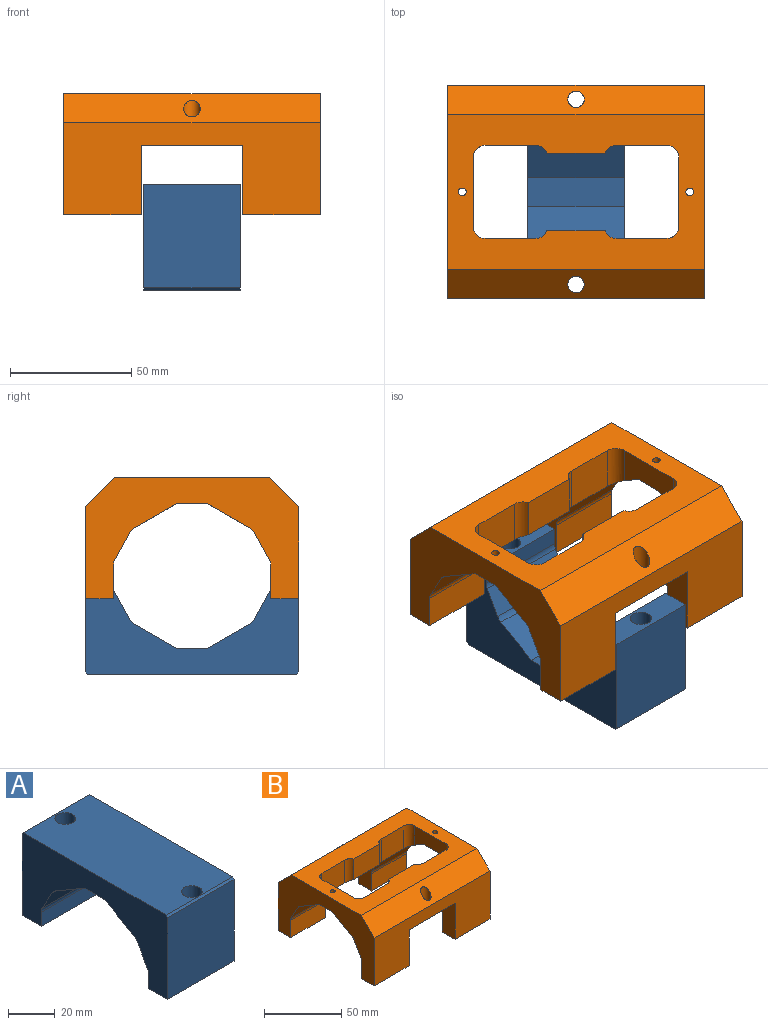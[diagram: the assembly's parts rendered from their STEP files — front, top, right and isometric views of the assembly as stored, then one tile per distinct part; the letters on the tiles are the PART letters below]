
ASSEMBLY  parts=2 mates=1
PART A: 22 faces, bbox 40x88x43.7 mm
  f0: plane 40x7.35mm, normal (0,-1,0), area 294.2mm2, adj f1,f15,f16,f17
  f1: plane 40x11.5mm, normal (0,0,-1), area 399.2mm2, adj f0,f2,f16,f17,f21
  f2: plane 42.65x40mm, normal (0,1,0), area 1706mm2, adj f1,f16,f17,f18
  f3: plane 86x40mm, normal (0,0,1), area 3318.4mm2, adj f16,f17,f18,f19,f20,f21
  f4: plane 42.65x40mm, normal (0,-1,0), area 1706mm2, adj f5,f16,f17,f19
  f5: plane 40x11.5mm, normal (0,0,-1), area 399.2mm2, adj f4,f6,f16,f17,f20
  f6: plane 40x7.35mm, normal (0,1,0), area 294.2mm2, adj f5,f7,f16,f17
  f7: cylinder r=5mm len=40mm, axis (-1,0,0), area 101.4mm2, adj f6,f8,f16,f17
  f8: plane 40x11.16mm, normal (0,0.87,-0.49), area 510.7mm2, adj f7,f9,f16,f17
  f9: cylinder r=5mm len=40mm, axis (-1,0,0), area 107.8mm2, adj f8,f10,f16,f17
  f10: plane 40x17.81mm, normal (0,0.5,-0.87), area 822.9mm2, adj f9,f11,f16,f17
  f11: plane 40x12mm, normal (0,0,-1), area 480mm2, adj f10,f12,f16,f17
  f12: plane 40x17.81mm, normal (0,-0.5,-0.87), area 822.9mm2, adj f11,f13,f16,f17
  f13: cylinder r=5mm len=40mm, axis (-1,0,0), area 107.8mm2, adj f12,f14,f16,f17
  f14: plane 40x11.16mm, normal (0,-0.87,-0.49), area 510.7mm2, adj f13,f15,f16,f17
  f15: cylinder r=5mm len=40mm, axis (-1,0,0), area 101.4mm2, adj f0,f14,f16,f17
  f16: plane 88x43.65mm, normal (1,0,0), area 2161.3mm2, adj f0,f1,f2,f3,f4,f5,f6,f7
  f17: plane 88x43.65mm, normal (-1,0,0), area 2161.3mm2, adj f0,f1,f2,f3,f4,f5,f6,f7
  f18: plane 40x1mm, normal (0,0.71,0.71), area 56.6mm2, adj f2,f3,f16,f17
  f19: plane 40x1mm, normal (0,-0.71,0.71), area 56.6mm2, adj f3,f4,f16,f17
  f20: cylinder r=4.4mm len=43.65mm, axis (0,0,-1), area 1206.7mm2, adj f3,f5
  f21: cylinder r=4.4mm len=43.65mm, axis (0,0,-1), area 1206.7mm2, adj f1,f3
PART B: 57 faces, bbox 107.4x89.4x51.4 mm
  f0: plane 32x11.5mm, normal (0,0,-1), area 368mm2, adj f4,f14,f22,f40
  f1: plane 32x11.5mm, normal (0,0,-1), area 368mm2, adj f5,f17,f22,f43
  f2: plane 32x11.16mm, normal (0,-0.87,-0.49), area 408.5mm2, adj f21,f41,f49,f52
  f3: plane 32x13.7mm, normal (0,-1,0), area 438.5mm2, adj f15,f21,f41,f49
  f4: plane 106x38mm, normal (0,1,0), area 2831mm2, adj f0,f15,f21,f22,f37,f39,f40,f41
  f5: plane 106x38mm, normal (0,-1,0), area 2831mm2, adj f1,f16,f21,f22,f38,f42,f43,f44
  f6: plane 32x13.7mm, normal (0,1,0), area 438.5mm2, adj f16,f21,f42,f50
  f7: plane 32x11.16mm, normal (0,0.87,-0.49), area 408.5mm2, adj f21,f42,f50,f51
  f8: plane 24x16.29mm, normal (0,1,0), area 390.9mm2, adj f10,f11,f32,f36
  f9: plane 24x16.29mm, normal (0,-1,0), area 390.9mm2, adj f10,f20,f29,f33
  f10: plane 106x64mm, normal (0,0,1), area 3689.5mm2, adj f8,f9,f21,f22,f23,f24,f25,f26
  f11: plane 107.22x20.22mm, normal (0,0.5,-0.87), area 1049.6mm2, adj f8,f12,f19,f21,f22,f23,f24,f27
  f12: plane 12x10.5mm, normal (0,0,-1), area 118mm2, adj f11,f20,f21,f24,f54
  f13: plane 32x11.16mm, normal (0,-0.87,-0.49), area 408.5mm2, adj f22,f40,f45,f48
  f14: plane 32x13.7mm, normal (0,-1,0), area 438.5mm2, adj f0,f22,f40,f45
  f15: plane 32x11.5mm, normal (0,0,-1), area 368mm2, adj f3,f4,f21,f41
  f16: plane 32x11.5mm, normal (0,0,-1), area 368mm2, adj f5,f6,f21,f42
  f17: plane 32x13.7mm, normal (0,1,0), area 438.5mm2, adj f1,f22,f43,f46
  f18: plane 32x11.16mm, normal (0,0.87,-0.49), area 408.5mm2, adj f22,f43,f46,f47
  f19: plane 12x10.5mm, normal (0,0,-1), area 118mm2, adj f11,f20,f22,f23,f53
  f20: plane 107.22x20.22mm, normal (0,-0.5,-0.87), area 1049.6mm2, adj f9,f12,f19,f21,f22,f23,f24,f25
  f21: plane 88x50mm, normal (1,0,0), area 2164.4mm2, adj f2,f3,f4,f5,f6,f7,f10,f11
  f22: plane 88x50mm, normal (-1,0,0), area 2164.4mm2, adj f0,f1,f4,f5,f10,f11,f13,f14
  f23: plane 28.5x15.28mm, normal (1,0,0), area 338.7mm2, adj f10,f11,f19,f20,f30,f31
  f24: plane 28.5x15.28mm, normal (-1,0,0), area 338.7mm2, adj f10,f11,f12,f20,f34,f35
  f25: plane 20.82x18.17mm, normal (0,-1,0), area 378.3mm2, adj f10,f20,f29,f30
  f26: plane 20.82x18.17mm, normal (0,-1,0), area 378.3mm2, adj f10,f20,f33,f34
  f27: plane 20.82x18.17mm, normal (0,1,0), area 378.3mm2, adj f10,f11,f35,f36
  f28: plane 20.82x18.17mm, normal (0,1,0), area 378.3mm2, adj f10,f11,f31,f32
  f29: cylinder r=5mm len=18.17mm, axis (0,0,1), area 104.5mm2, adj f9,f10,f20,f25
  f30: cylinder r=5mm len=18.17mm, axis (0,0,1), area 131.3mm2, adj f10,f20,f23,f25
  f31: cylinder r=5mm len=18.17mm, axis (0,0,-1), area 131.3mm2, adj f10,f11,f23,f28
  f32: cylinder r=5mm len=18.17mm, axis (0,0,-1), area 104.5mm2, adj f8,f10,f11,f28
  f33: cylinder r=5mm len=18.17mm, axis (0,0,1), area 104.5mm2, adj f9,f10,f20,f26
  f34: cylinder r=5mm len=18.17mm, axis (0,0,1), area 131.3mm2, adj f10,f20,f24,f26
  f35: cylinder r=5mm len=18.17mm, axis (0,0,-1), area 131.3mm2, adj f10,f11,f24,f27
  f36: cylinder r=5mm len=18.17mm, axis (0,0,-1), area 104.5mm2, adj f8,f10,f11,f27
  f37: plane 107.43x13.43mm, normal (0,0.71,0.71), area 1747.5mm2, adj f4,f10,f21,f22,f56
  f38: plane 107.43x13.43mm, normal (0,-0.71,0.71), area 1747.5mm2, adj f5,f10,f21,f22,f55
  f39: plane 42x19mm, normal (0,0,-1), area 761.7mm2, adj f4,f20,f40,f41,f56
  f40: plane 29.19x20.2mm, normal (1,0,0), area 378.7mm2, adj f0,f4,f13,f14,f20,f39,f45,f48
  f41: plane 29.19x20.2mm, normal (-1,0,0), area 378.7mm2, adj f2,f3,f4,f15,f20,f39,f49,f52
  f42: plane 29.19x20.2mm, normal (-1,0,0), area 378.7mm2, adj f5,f6,f7,f11,f16,f44,f50,f51
  f43: plane 29.19x20.2mm, normal (1,0,0), area 378.7mm2, adj f1,f5,f11,f17,f18,f44,f46,f47
  f44: plane 42x19mm, normal (0,0,-1), area 761.7mm2, adj f5,f11,f42,f43,f55
  f45: cylinder r=5mm len=32mm, axis (1,0,0), area 81.1mm2, adj f13,f14,f22,f40
  f46: cylinder r=5mm len=32mm, axis (1,0,0), area 81.1mm2, adj f17,f18,f22,f43
  f47: cylinder r=5mm len=32mm, axis (1,0,0), area 86.2mm2, adj f11,f18,f22,f43
  f48: cylinder r=5mm len=32mm, axis (1,0,0), area 86.2mm2, adj f13,f20,f22,f40
  f49: cylinder r=5mm len=32mm, axis (1,0,0), area 81.1mm2, adj f2,f3,f21,f41
  f50: cylinder r=5mm len=32mm, axis (1,0,0), area 81.1mm2, adj f6,f7,f21,f42
  f51: cylinder r=5mm len=32mm, axis (1,0,0), area 86.2mm2, adj f7,f11,f21,f42
  f52: cylinder r=5mm len=32mm, axis (1,0,0), area 86.2mm2, adj f2,f20,f21,f41
  f53: cylinder r=1.6mm len=10.5mm, axis (0,0,1), area 105.6mm2, adj f10,f19
  f54: cylinder r=1.6mm len=10.5mm, axis (0,0,1), area 105.6mm2, adj f10,f12
  f55: cylinder r=3.4mm len=18.67mm, axis (0,0,-1), area 328.3mm2, adj f38,f44
  f56: cylinder r=3.4mm len=18.67mm, axis (0,0,-1), area 328.3mm2, adj f37,f39
PLACE A rot(axis=(1,0,0),180deg) t=(0,0.24,-45.06)mm
PLACE B t=(0,-0.15,-16.35)mm
MATE fastened A.f1 <-> B.f55  axis (0,0,1) through (0,-38.4,-29.02)mm
